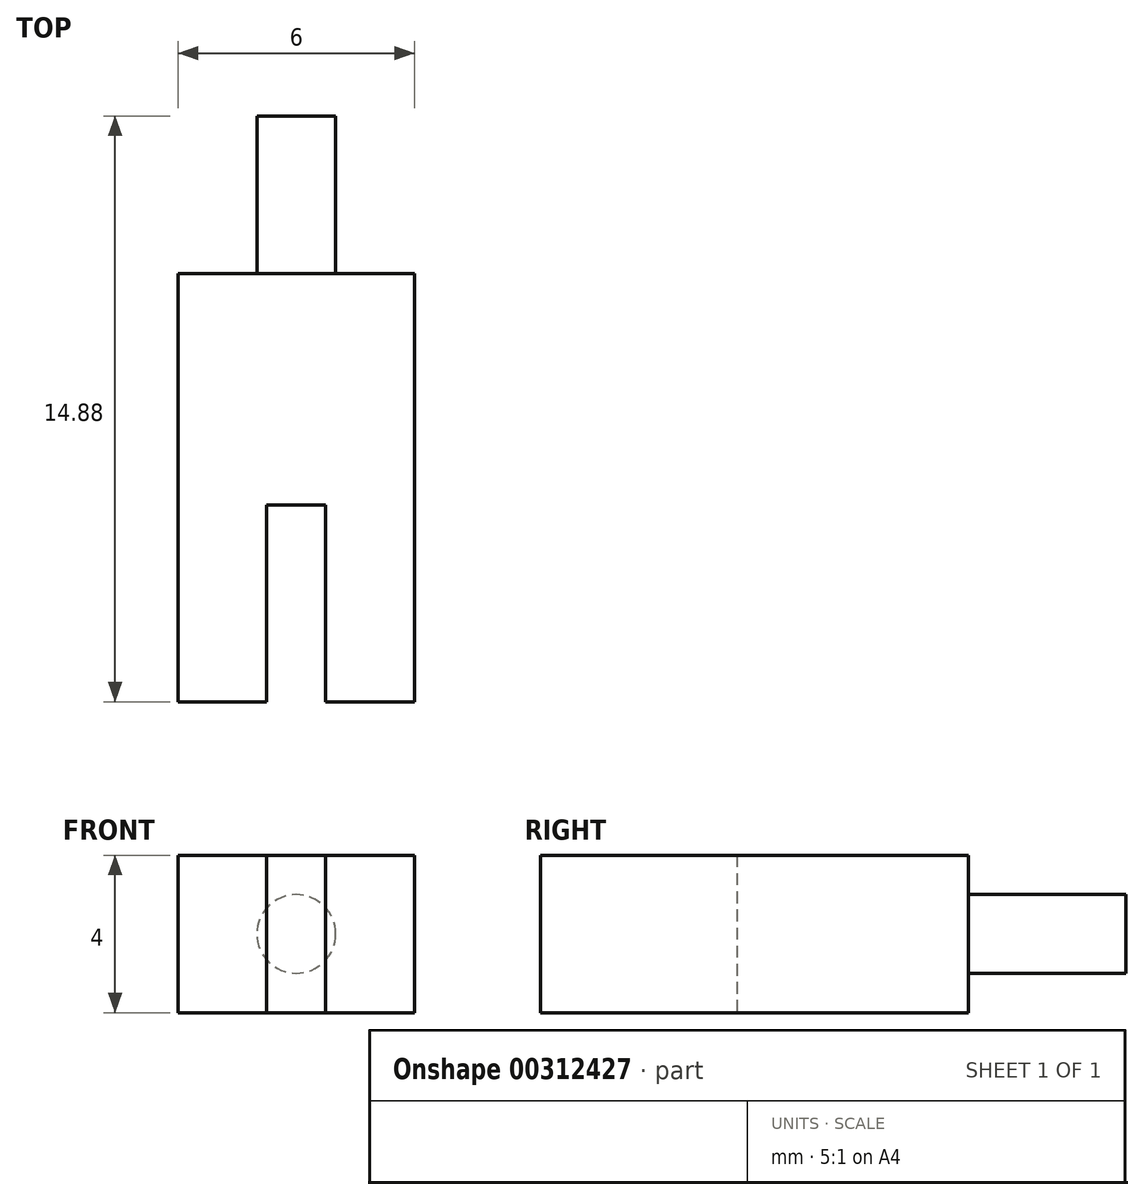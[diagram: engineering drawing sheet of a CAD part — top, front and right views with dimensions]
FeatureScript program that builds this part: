
annotation { "Feature Type Name" : "Feature", "Feature Type Description" : "" }
export const myFeature = defineFeature(function(context is Context, id is Id, definition is map)
    precondition{}
    {
        {
            var Q0;
            Q0=qCreatedBy(makeId("Top.planeOp"),FACE);
            var sketch = newSketch(context, id + "F0", { "sketchPlane" : qUnion([Q0])});
            skLineSegment(sketch, "E0.top", {"start": v(-3.75, -27) * mm, "end": v(-2.25, -27) * mm});
            skLineSegment(sketch, "E0.left", {"start": v(-3.75, -32) * mm, "end": v(-3.75, -27) * mm});
            skLineSegment(sketch, "E0.right", {"start": v(-2.25, -32) * mm, "end": v(-2.25, -27) * mm});
            skLineSegment(sketch, "E1", {"start": v(-6, -21.12) * mm, "end": v(-6, -21.12) * mm});
            skLineSegment(sketch, "E2", {"start": v(-6, -21.12) * mm, "end": v(0, -21.12) * mm});
            skLineSegment(sketch, "E3", {"start": v(-6, -21.12) * mm, "end": v(-6, -32) * mm});
            skLineSegment(sketch, "E4", {"start": v(0, -21.12) * mm, "end": v(0, -21.28) * mm});
            skLineSegment(sketch, "E5", {"start": v(0, -21.28) * mm, "end": v(0, -32) * mm});
            skLineSegment(sketch, "E6", {"start": v(-6, -32) * mm, "end": v(-3.75, -32) * mm});
            skLineSegment(sketch, "E7", {"start": v(-2.25, -32) * mm, "end": v(0, -32) * mm});
            skSolve(sketch);
        }
        {
            var Q0;
            Q0 = qSketchRegion(id + "F0", true);
            extrude(context, id + "F1", {"entities" : qUnion([Q0]), "depth" : 4 * mm});
        }
        {
            var Q0;
            Q0=makeQuery(id+"F1.opExtrude","SWEPT_FACE",FACE,{"disambiguationData":[OSD([sQuery(id+"F0.wireOp",EDGE,"E2")])]});
            var sketch = newSketch(context, id + "F2", { "sketchPlane" : qUnion([Q0])});
            skLineSegment(sketch, "E8", {"start": v(3, 4) * mm, "end": v(3, 0) * mm, "construction": true});
            skCircle(sketch, "E9", {"center": v(3, 2) * mm, "radius": 1 * mm});
            skSolve(sketch);
        }
        {
            var Q0;
            Q0 = qSketchRegion(id + "F2", true);
            extrude(context, id + "F3", {"entities" : qUnion([Q0]), "operationType" : NewBodyOperationType.ADD, "depth" : 4 * mm});
        }
    });
